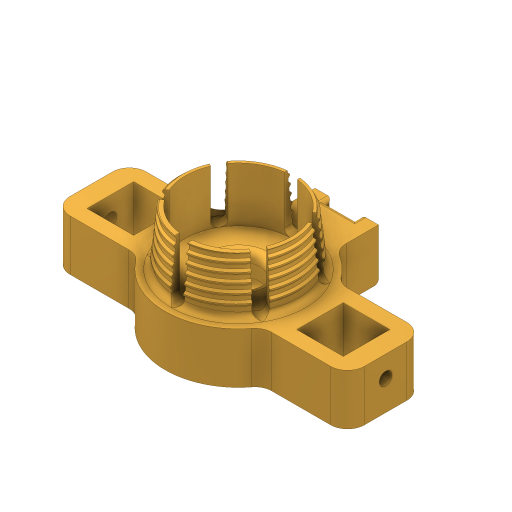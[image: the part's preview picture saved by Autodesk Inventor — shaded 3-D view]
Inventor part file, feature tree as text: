
AUTODESK INVENTOR PART (.ipt)
format: ipt  version: 2023 (Build 270158000, 158)  size: 1,296,896 bytes
history: native  units: mm
features: sketch x7, extrude x5, fillet x4, hole x3, helix x2, direct_edit x2, draft x1, mirror x1, other x1, revolve x1
ambient origin geometry x8: Origin, YZ Plane, XZ Plane, XY Plane, X Axis, Y Axis, Z Axis, Center Point
bodies: Solid1 (feature_tree)
feature tree (27):
  extrude  "Extrusion1"  Depth=26.5mm
  draft  "FaceDraft1"
  sketch  "Sketch2"  dims[d34=0.0mm d35=0.0mm d56=8.726646mm]
  helix  "Coil3"  [1 undecoded]
  helix  "Coil4"  [1 undecoded]
  direct_edit  "Direct Edit2"
  extrude  "Extrusion2"  Depth=8.726646mm
  extrude  "Extrusion13"  TaperAngle=90.0deg  [1 undecoded]
  extrude  "Extrusion14"  Depth=34.58632mm
  hole  "Hole3"  [1 undecoded]
  hole  "Hole4"  [1 undecoded]
  fillet  "Fillet11"  Radius=60.0mm
  fillet  "Fillet12"  [1 undecoded]
  hole  "Hole5"  [1 undecoded]
  mirror  "Mirror2"
  extrude  "Extrusion15"  Depth=1.5mm
  direct_edit  "Direct Edit3"
  fillet  "Fillet13"  Radius=18.0mm
  fillet  "Fillet15"  Radius=11.0mm
  sketch  "Sketch1"  dims[d0=25.0mm d1=26.5mm d2=12.875mm d3=0.0mm d4=1.047198mm]
  sketch  "Sketch3"  dims[d62=2.0mm d63=10.15mm d64=10.0mm d65=1.047198mm]
  sketch  "Sketch13"  dims[d66=90.0deg d67=90.0deg d68=0.0mm d69=0.0mm d70=2.0mm d71=3.0mm d72=10.0mm d73=-1.047198mm d74=90.0deg d75=90.0deg d76=0.0mm d77=0.0mm]
  sketch  "Sketch14"  dims[d79=-0.127mm d145=34.58632mm]
  sketch  "Sketch15"  dims[d150=120.0deg d151=120.0deg]
  sketch  "Sketch16"  dims[d153=21.6866mm d157=12.0mm d158=0.0mm d160=60.0mm d162=360.0deg d164=0.0mm d165=0.0mm d179=5.3mm d180=6.0mm d181=4.0mm d182=2.0mm d183=90.0deg d184=5.0mm d185=0.0mm d186=10.0mm d187=6.0mm d188=4.0mm d189=2.0mm d190=90.0deg d191=7.0mm d192=0.0mm d193=2.0mm d194=20.0mm d195=18.0mm d196=11.0mm d197=10.0mm d198=4.0mm d199=3.0mm d200=6.0mm d201=3.01mm d202=2.0mm d203=14.3117mm d204=8.0mm d205=0.0mm d206=15.0mm d207=10.0mm d208=7.0mm d209=10.0mm d210=1.0mm d211=0.0mm d212=-4.363323mm d213=1.0mm d215=1.5mm d109=0.5mm d110=0.872665mm d111=0.5mm d112=0.872665mm]
  other  "Size2"
  revolve  "Rotate1"  [1 undecoded]
note: 8 required parameter values undecoded (feature->parameter linkage not recoverable at this tier; creation-order binding heuristic only, values carry confidence <= 0.55)